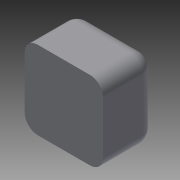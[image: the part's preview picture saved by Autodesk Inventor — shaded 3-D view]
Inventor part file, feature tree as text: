
AUTODESK INVENTOR PART (.ipt)
format: ipt  version: 2015 (Build 190159000, 159)  size: 93,184 bytes
history: native  units: in
note: dims shown in document units (in); Inventor stores cm internally (conversion verified against a paired STEP export)
features: extrude x1, fillet x1, sketch x1
ambient origin geometry x8: Origin, YZ Plane, XZ Plane, XY Plane, X Axis, Y Axis, Z Axis, Center Point
bodies: Solid1 (feature_tree)
feature tree (3):
  extrude  "Extrusion1"  Depth=0.75in
  fillet  "Fillet1"  Radius=0.5in
  sketch  "Sketch1"  dims[d0=0.75in d1=0.75in d2=0.5in d3=0.0in d4=0.125in]
